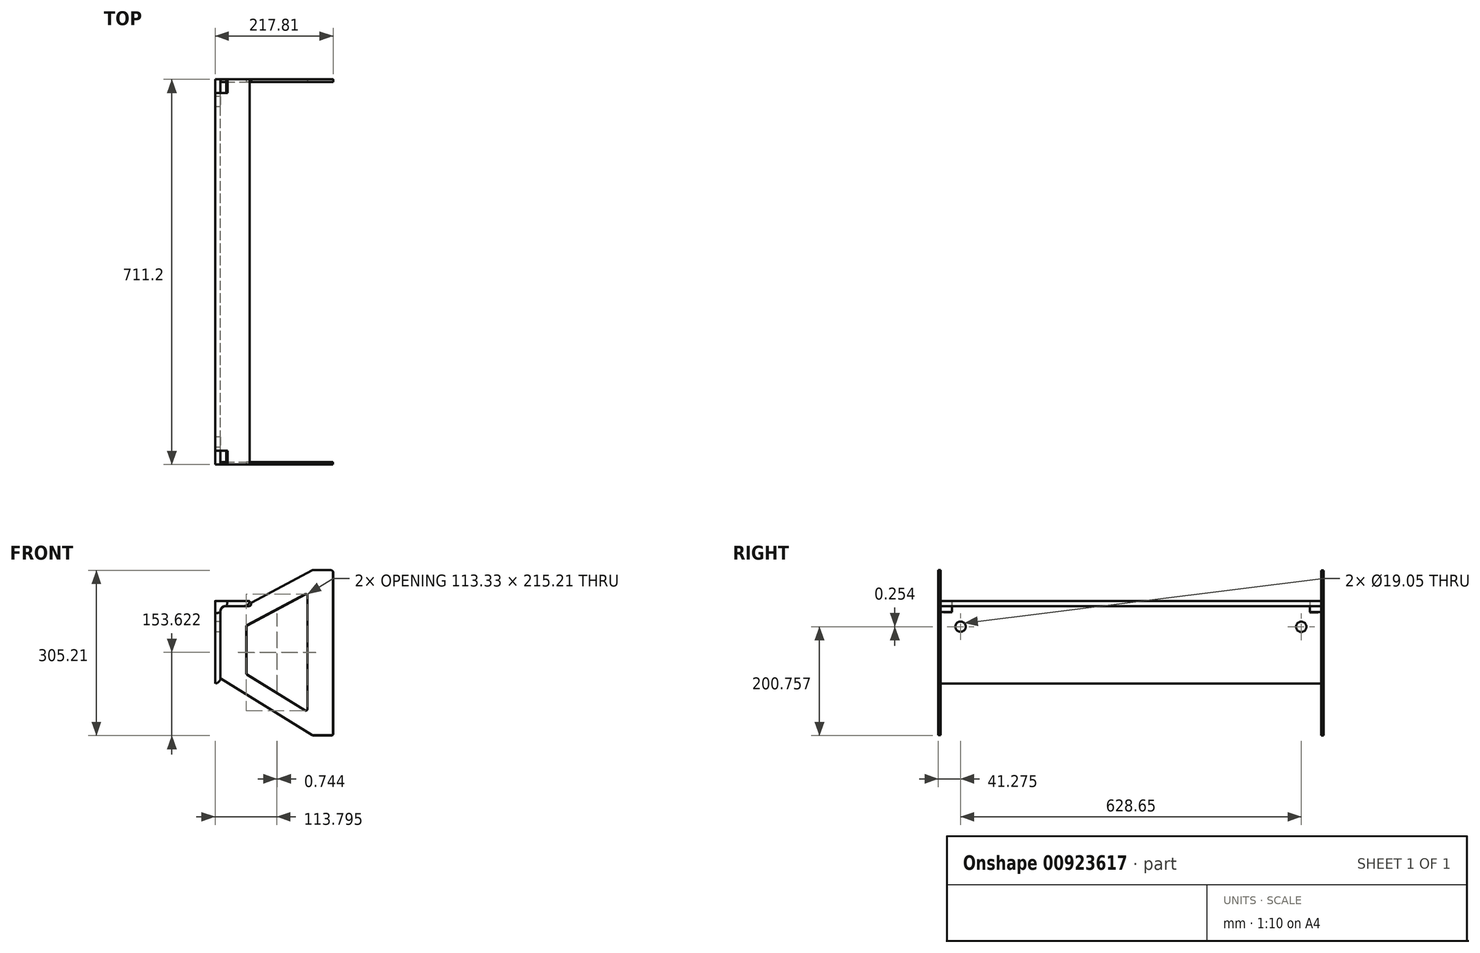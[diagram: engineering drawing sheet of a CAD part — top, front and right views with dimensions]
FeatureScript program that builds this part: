
annotation { "Feature Type Name" : "Feature", "Feature Type Description" : "" }
export const myFeature = defineFeature(function(context is Context, id is Id, definition is map)
    precondition{}
    {
        {
            var Q0;
            Q0=qCreatedBy(makeId("Front.planeOp"),FACE);
            var sketch = newSketch(context, id + "F0", { "sketchPlane" : qUnion([Q0])});
            skLineSegment(sketch, "E0", {"start": v(-47.1, 105) * mm, "end": v(-47.1, -47.15) * mm});
            skLineSegment(sketch, "E1", {"start": v(-47.1, -47.15) * mm, "end": v(-47.1, -47.15) * mm});
            skLineSegment(sketch, "E2", {"start": v(-37.57, -37.63) * mm, "end": v(-37.57, 86.2) * mm});
            skLineSegment(sketch, "E3", {"start": v(-28.05, 95.72) * mm, "end": v(6.88, 95.72) * mm});
            skLineSegment(sketch, "E4", {"start": v(-46.84, 105.25) * mm, "end": v(16.4, 105.25) * mm});
            skLineSegment(sketch, "E5", {"start": v(16.4, 105.25) * mm, "end": v(16.4, 105.25) * mm});
            skPoint(sketch, "E6.visualSharp", {"position": v(-37.57, 95.72) * mm});
            skArc(sketch, "E6.filletArc", {"start": v(-28.05, 95.72) * mm, "mid": v(-34.78, 92.93) * mm, "end": v(-37.57, 86.2) * mm});
            skPoint(sketch, "E7.visualSharp", {"position": v(-37.57, -47.15) * mm});
            skArc(sketch, "E7.filletArc", {"start": v(-47.1, -47.15) * mm, "mid": v(-40.36, -44.36) * mm, "end": v(-37.57, -37.63) * mm});
            skPoint(sketch, "E8.visualSharp", {"position": v(16.4, 95.72) * mm});
            skArc(sketch, "E8.filletArc", {"start": v(6.88, 95.72) * mm, "mid": v(13.61, 98.51) * mm, "end": v(16.4, 105.25) * mm});
            skPoint(sketch, "E9.visualSharp", {"position": v(-47.1, 105.25) * mm});
            skArc(sketch, "E9.filletArc", {"start": v(-46.84, 105.25) * mm, "mid": v(-47.02, 105.17) * mm, "end": v(-47.1, 105) * mm});
            skSolve(sketch);
        }
        {
            var Q0;
            Q0=makeQuery(id+"F0.imprint","IMPRINT",FACE,{"disambiguationData":[TD([[makeQuery(id+"F0.imprint","IMPRINT",EDGE,{"derivedFrom":sQuery(id+"F0.wireOp",EDGE,"E0")}),1.0]])]});
            extrude(context, id + "F1", {"entities" : qUnion([Q0]), "depth" : 711.2 * mm, "offsetDistance" : 25.4 * mm});
        }
        {
            var Q0;
            Q0=makeQuery(id+"F1.opExtrude","CAP_FACE",FACE,{"disambiguationData":[OSD([sQuery(id+"F0.wireOp",EDGE,"E0"),sQuery(id+"F0.wireOp",EDGE,"E2"),sQuery(id+"F0.wireOp",EDGE,"E3"),sQuery(id+"F0.wireOp",EDGE,"E4"),sQuery(id+"F0.wireOp",EDGE,"E6.filletArc"),sQuery(id+"F0.wireOp",EDGE,"E7.filletArc"),sQuery(id+"F0.wireOp",EDGE,"E8.filletArc"),sQuery(id+"F0.wireOp",EDGE,"E9.filletArc")])],"isStart":false});
            var sketch = newSketch(context, id + "F2", { "sketchPlane" : qUnion([Q0])});
            skCircle(sketch, "E10", {"center": v(-46.67, 104.81) * mm, "radius": 22.23 * mm});
            skSolve(sketch);
        }
        {
            var Q0;
            Q0=qSketchRegion(id+"F2",true);
            extrude(context, id + "F3", {"entities" : qUnion([Q0]), "operationType" : NewBodyOperationType.REMOVE, "oppositeDirection" : true, "depth" : 25.4 * mm, "offsetDistance" : 25.4 * mm});
        }
        {
            var Q0;
            Q0=makeQuery(id+"F1.opExtrude","CAP_FACE",FACE,{"disambiguationData":[OSD([sQuery(id+"F0.wireOp",EDGE,"E0"),sQuery(id+"F0.wireOp",EDGE,"E2"),sQuery(id+"F0.wireOp",EDGE,"E3"),sQuery(id+"F0.wireOp",EDGE,"E4"),sQuery(id+"F0.wireOp",EDGE,"E6.filletArc"),sQuery(id+"F0.wireOp",EDGE,"E7.filletArc"),sQuery(id+"F0.wireOp",EDGE,"E8.filletArc"),sQuery(id+"F0.wireOp",EDGE,"E9.filletArc")])],"isStart":true});
            var sketch = newSketch(context, id + "F4", { "sketchPlane" : qUnion([Q0])});
            skCircle(sketch, "E11", {"center": v(46.67, 104.81) * mm, "radius": 22.23 * mm});
            skSolve(sketch);
        }
        {
            var Q0;
            Q0=qSketchRegion(id+"F4",true);
            extrude(context, id + "F5", {"entities" : qUnion([Q0]), "operationType" : NewBodyOperationType.REMOVE, "oppositeDirection" : true, "depth" : 25.4 * mm, "offsetDistance" : 25.4 * mm});
        }
        {
            var Q0;
            Q0=makeQuery(id+"F1.opExtrude","SWEPT_FACE",FACE,{"disambiguationData":[OSD([sQuery(id+"F0.wireOp",EDGE,"E0")])]});
            var sketch = newSketch(context, id + "F6", { "sketchPlane" : qUnion([Q0])});
            skCircle(sketch, "E12", {"center": v(41.27, 57.37) * mm, "radius": 9.53 * mm});
            skCircle(sketch, "E13", {"center": v(669.93, 57.62) * mm, "radius": 9.53 * mm});
            skSolve(sketch);
        }
        {
            var Q0;
            Q0=qSketchRegion(id+"F6",true);
            extrude(context, id + "F7", {"entities" : qUnion([Q0]), "operationType" : NewBodyOperationType.REMOVE, "endBound" : BoundingType.THROUGH_ALL, "oppositeDirection" : true, "depth" : 25.4 * mm, "offsetDistance" : 25.4 * mm});
        }
        {
            var Q0;
            {var subQ0=sQuery(id+"F0.wireOp",EDGE,"E0");var subQ1=sQuery(id+"F0.wireOp",EDGE,"E2");var subQ2=sQuery(id+"F0.wireOp",EDGE,"E7.filletArc");Q0=makeQuery(id+"F3.boolean.opBoolean","SPLIT",FACE,{"disambiguationData":[TD([makeQuery(id+"F1.opExtrude","SWEPT_FACE",FACE,{"disambiguationData":[OSD([subQ0])]})])],"derivedFrom":makeQuery(id+"F1.opExtrude","CAP_FACE",FACE,{"disambiguationData":[OSD([subQ0,subQ1,sQuery(id+"F0.wireOp",EDGE,"E3"),sQuery(id+"F0.wireOp",EDGE,"E4"),sQuery(id+"F0.wireOp",EDGE,"E6.filletArc"),subQ2,sQuery(id+"F0.wireOp",EDGE,"E8.filletArc"),sQuery(id+"F0.wireOp",EDGE,"E9.filletArc")])],"isStart":false})});}
            var sketch = newSketch(context, id + "F8", { "sketchPlane" : qUnion([Q0])});
            skLineSegment(sketch, "E14", {"start": v(20.8, 102.68) * mm, "end": v(131.17, 161.45) * mm});
            skLineSegment(sketch, "E15", {"start": v(132.66, 161.82) * mm, "end": v(166.79, 161.82) * mm});
            skLineSegment(sketch, "E16", {"start": v(169.96, 158.65) * mm, "end": v(169.96, -139.8) * mm});
            skLineSegment(sketch, "E17", {"start": v(166.79, -142.98) * mm, "end": v(133.47, -142.98) * mm});
            skLineSegment(sketch, "E18", {"start": v(131.8, -142.5) * mm, "end": v(-36.07, -38.56) * mm});
            skLineSegment(sketch, "E19", {"start": v(-37.57, -35.86) * mm, "end": v(-37.57, 84.53) * mm});
            skArc(sketch, "E20", {"start": v(-26.54, 95.76) * mm, "mid": v(-34.35, 92.4) * mm, "end": v(-37.57, 84.53) * mm});
            skLineSegment(sketch, "E21", {"start": v(123.36, 114.66) * mm, "end": v(123.36, -94.2) * mm});
            skLineSegment(sketch, "E22", {"start": v(118.51, -96.9) * mm, "end": v(11.53, -30.66) * mm});
            skLineSegment(sketch, "E23", {"start": v(10.03, -27.96) * mm, "end": v(10.03, 57.69) * mm});
            skLineSegment(sketch, "E24", {"start": v(11.71, 60.5) * mm, "end": v(118.7, 117.47) * mm});
            skPoint(sketch, "E25.visualSharp", {"position": v(131.86, 161.82) * mm});
            skArc(sketch, "E25.filletArc", {"start": v(132.66, 161.82) * mm, "mid": v(131.89, 161.73) * mm, "end": v(131.17, 161.45) * mm});
            skPoint(sketch, "E26.visualSharp", {"position": v(169.96, 161.82) * mm});
            skArc(sketch, "E26.filletArc", {"start": v(169.96, 158.65) * mm, "mid": v(169.04, 160.9) * mm, "end": v(166.79, 161.82) * mm});
            skPoint(sketch, "E27.visualSharp", {"position": v(123.36, 119.95) * mm});
            skArc(sketch, "E27.filletArc", {"start": v(123.36, 114.66) * mm, "mid": v(121.82, 117.39) * mm, "end": v(118.7, 117.47) * mm});
            skPoint(sketch, "E28.visualSharp", {"position": v(10.03, 59.6) * mm});
            skArc(sketch, "E28.filletArc", {"start": v(11.71, 60.5) * mm, "mid": v(10.48, 59.32) * mm, "end": v(10.03, 57.69) * mm});
            skPoint(sketch, "E29.visualSharp", {"position": v(10.03, -29.73) * mm});
            skArc(sketch, "E29.filletArc", {"start": v(10.03, -27.96) * mm, "mid": v(10.43, -29.5) * mm, "end": v(11.53, -30.66) * mm});
            skPoint(sketch, "E30.visualSharp", {"position": v(123.36, -99.9) * mm});
            skArc(sketch, "E30.filletArc", {"start": v(118.51, -96.9) * mm, "mid": v(121.73, -96.97) * mm, "end": v(123.36, -94.2) * mm});
            skPoint(sketch, "E31.visualSharp", {"position": v(169.96, -142.98) * mm});
            skArc(sketch, "E31.filletArc", {"start": v(166.79, -142.98) * mm, "mid": v(169.04, -142.05) * mm, "end": v(169.96, -139.8) * mm});
            skPoint(sketch, "E32.visualSharp", {"position": v(132.56, -142.98) * mm});
            skArc(sketch, "E32.filletArc", {"start": v(131.8, -142.5) * mm, "mid": v(132.6, -142.86) * mm, "end": v(133.47, -142.98) * mm});
            skPoint(sketch, "E33.visualSharp", {"position": v(-37.57, -37.63) * mm});
            skArc(sketch, "E33.filletArc", {"start": v(-37.57, -35.86) * mm, "mid": v(-37.17, -37.4) * mm, "end": v(-36.07, -38.56) * mm});
            skPoint(sketch, "E34.visualSharp", {"position": v(11.42, 101.78) * mm});
            skArc(sketch, "E34.filletArc", {"start": v(11.67, 101.78) * mm, "mid": v(11.42, 101.77) * mm, "end": v(11.17, 101.74) * mm});
            skLineSegment(sketch, "E35", {"start": v(-26.54, 95.76) * mm, "end": v(15.95, 95.76) * mm});
            skLineSegment(sketch, "E36", {"start": v(19.12, 99.87) * mm, "end": v(19.12, 98.93) * mm});
            skPoint(sketch, "E37.visualSharp", {"position": v(19.12, 101.78) * mm});
            skArc(sketch, "E37.filletArc", {"start": v(20.8, 102.68) * mm, "mid": v(19.58, 101.5) * mm, "end": v(19.12, 99.87) * mm});
            skPoint(sketch, "E38.visualSharp", {"position": v(19.12, 95.76) * mm});
            skArc(sketch, "E38.filletArc", {"start": v(15.95, 95.76) * mm, "mid": v(18.2, 96.69) * mm, "end": v(19.12, 98.93) * mm});
            skSolve(sketch);
        }
        {
            var Q0;
            Q0=makeQuery(id+"F8.imprint","IMPRINT",FACE,{"disambiguationData":[TD([[makeQuery(id+"F8.imprint","IMPRINT",EDGE,{"derivedFrom":sQuery(id+"F8.wireOp",EDGE,"E14")}),-1.0]])]});
            extrude(context, id + "F9", {"entities" : qUnion([Q0]), "oppositeDirection" : true, "depth" : 4.57 * mm, "offsetDistance" : 25.4 * mm});
        }
        {
            var Q0;
            Q0=qCreatedBy(makeId("Front.planeOp"),FACE);
            var sketch = newSketch(context, id + "F10", { "sketchPlane" : qUnion([Q0])});
            skLineSegment(sketch, "E39", {"start": v(21.55, 102.26) * mm, "end": v(131.9, 161.04) * mm});
            skLineSegment(sketch, "E40", {"start": v(133.4, 161.4) * mm, "end": v(167.53, 161.4) * mm});
            skLineSegment(sketch, "E41", {"start": v(170.7, 158.23) * mm, "end": v(170.7, -140.22) * mm});
            skLineSegment(sketch, "E42", {"start": v(167.53, -143.4) * mm, "end": v(134.21, -143.4) * mm});
            skLineSegment(sketch, "E43", {"start": v(132.54, -142.92) * mm, "end": v(-35.33, -38.97) * mm});
            skLineSegment(sketch, "E44", {"start": v(-36.83, -36.27) * mm, "end": v(-36.83, 84.12) * mm});
            skArc(sketch, "E45", {"start": v(-25.8, 95.34) * mm, "mid": v(-33.61, 91.99) * mm, "end": v(-36.83, 84.12) * mm});
            skLineSegment(sketch, "E46", {"start": v(124.1, 114.25) * mm, "end": v(124.1, -94.61) * mm});
            skLineSegment(sketch, "E47", {"start": v(119.26, -97.31) * mm, "end": v(12.28, -31.07) * mm});
            skLineSegment(sketch, "E48", {"start": v(10.77, -28.37) * mm, "end": v(10.77, 57.27) * mm});
            skLineSegment(sketch, "E49", {"start": v(12.46, 60.08) * mm, "end": v(119.44, 117.05) * mm});
            skPoint(sketch, "E50.visualSharp", {"position": v(132.6, 161.4) * mm});
            skArc(sketch, "E50.filletArc", {"start": v(133.4, 161.4) * mm, "mid": v(132.63, 161.31) * mm, "end": v(131.9, 161.04) * mm});
            skPoint(sketch, "E51.visualSharp", {"position": v(170.7, 161.4) * mm});
            skArc(sketch, "E51.filletArc", {"start": v(170.7, 158.23) * mm, "mid": v(169.78, 160.48) * mm, "end": v(167.53, 161.4) * mm});
            skPoint(sketch, "E52.visualSharp", {"position": v(124.1, 119.54) * mm});
            skArc(sketch, "E52.filletArc", {"start": v(124.1, 114.25) * mm, "mid": v(122.56, 116.97) * mm, "end": v(119.44, 117.05) * mm});
            skPoint(sketch, "E53.visualSharp", {"position": v(10.77, 59.18) * mm});
            skArc(sketch, "E53.filletArc", {"start": v(12.46, 60.08) * mm, "mid": v(11.23, 58.9) * mm, "end": v(10.77, 57.27) * mm});
            skPoint(sketch, "E54.visualSharp", {"position": v(10.77, -30.14) * mm});
            skArc(sketch, "E54.filletArc", {"start": v(10.77, -28.37) * mm, "mid": v(11.17, -29.92) * mm, "end": v(12.28, -31.07) * mm});
            skPoint(sketch, "E55.visualSharp", {"position": v(124.1, -100.32) * mm});
            skArc(sketch, "E55.filletArc", {"start": v(119.26, -97.31) * mm, "mid": v(122.47, -97.39) * mm, "end": v(124.1, -94.61) * mm});
            skPoint(sketch, "E56.visualSharp", {"position": v(170.7, -143.4) * mm});
            skArc(sketch, "E56.filletArc", {"start": v(167.53, -143.4) * mm, "mid": v(169.78, -142.46) * mm, "end": v(170.7, -140.22) * mm});
            skPoint(sketch, "E57.visualSharp", {"position": v(133.3, -143.4) * mm});
            skArc(sketch, "E57.filletArc", {"start": v(132.54, -142.92) * mm, "mid": v(133.34, -143.27) * mm, "end": v(134.21, -143.4) * mm});
            skPoint(sketch, "E58.visualSharp", {"position": v(-36.83, -38.04) * mm});
            skArc(sketch, "E58.filletArc", {"start": v(-36.83, -36.27) * mm, "mid": v(-36.43, -37.82) * mm, "end": v(-35.33, -38.97) * mm});
            skPoint(sketch, "E59.visualSharp", {"position": v(12.16, 101.36) * mm});
            skArc(sketch, "E59.filletArc", {"start": v(12.41, 101.36) * mm, "mid": v(12.16, 101.36) * mm, "end": v(11.91, 101.33) * mm});
            skLineSegment(sketch, "E60", {"start": v(-25.8, 95.34) * mm, "end": v(16.7, 95.34) * mm});
            skLineSegment(sketch, "E61", {"start": v(19.87, 99.46) * mm, "end": v(19.87, 98.52) * mm});
            skPoint(sketch, "E62.visualSharp", {"position": v(19.87, 101.36) * mm});
            skArc(sketch, "E62.filletArc", {"start": v(21.55, 102.26) * mm, "mid": v(20.32, 101.1) * mm, "end": v(19.87, 99.46) * mm});
            skPoint(sketch, "E63.visualSharp", {"position": v(19.87, 95.34) * mm});
            skArc(sketch, "E63.filletArc", {"start": v(16.7, 95.34) * mm, "mid": v(18.94, 96.27) * mm, "end": v(19.87, 98.52) * mm});
            skSolve(sketch);
        }
        {
            var Q0;
            Q0=makeQuery(id+"F10.imprint","IMPRINT",FACE,{"disambiguationData":[TD([[makeQuery(id+"F10.imprint","IMPRINT",EDGE,{"derivedFrom":sQuery(id+"F10.wireOp",EDGE,"E39")}),-1.0]])]});
            extrude(context, id + "F11", {"entities" : qUnion([Q0]), "depth" : 4.57 * mm, "offsetDistance" : 25.4 * mm});
        }
    });
